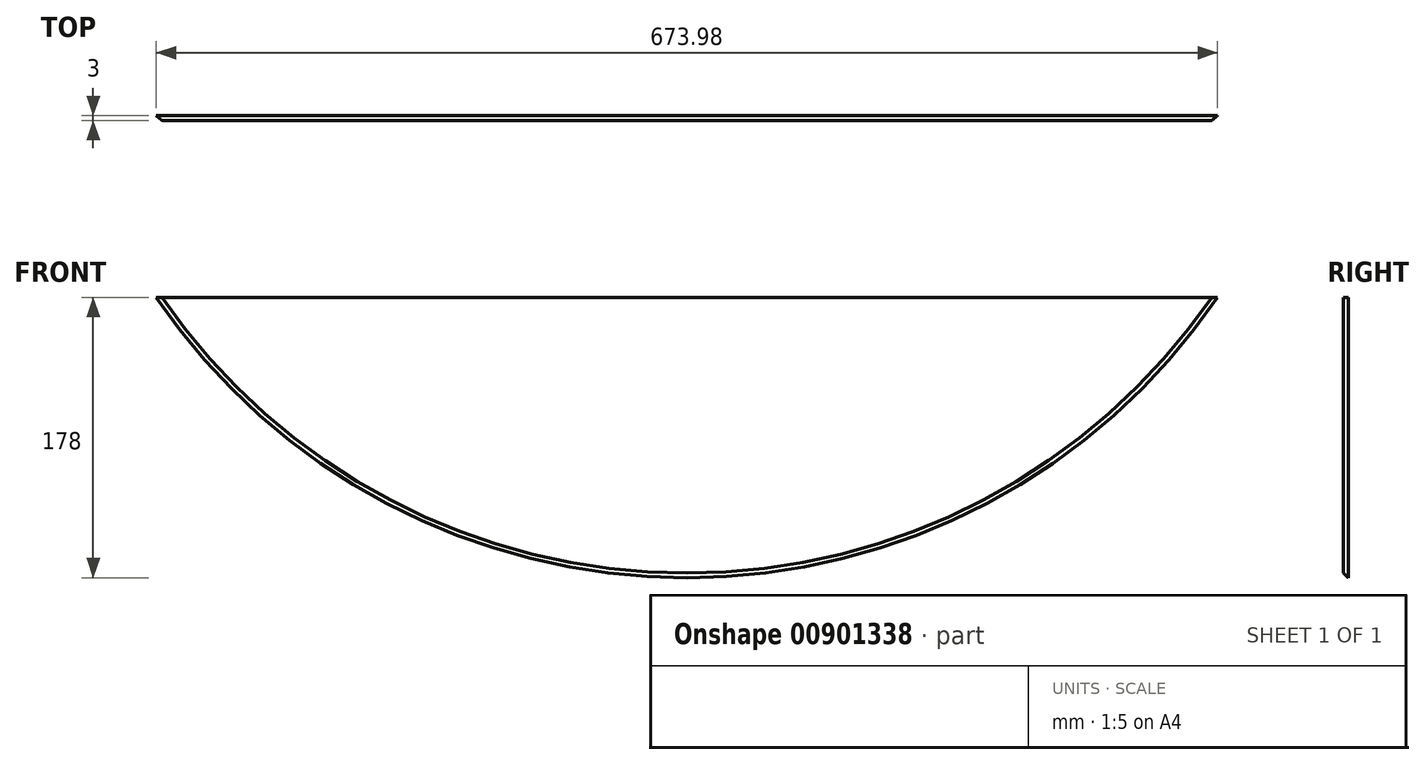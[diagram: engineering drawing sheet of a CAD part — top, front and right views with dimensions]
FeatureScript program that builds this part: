
annotation { "Feature Type Name" : "Feature", "Feature Type Description" : "" }
export const myFeature = defineFeature(function(context is Context, id is Id, definition is map)
    precondition{}
    {
        {
            var Q0;
            Q0=qCreatedBy(makeId("Front.planeOp"),FACE);
            var sketch = newSketch(context, id + "F0", { "sketchPlane" : qUnion([Q0])});
            skArc(sketch, "E0", {"start": v(-339.41, 0) * mm, "mid": v(0, -180) * mm, "end": v(339.41, 0) * mm});
            skLineSegment(sketch, "E1", {"start": v(0, 0) * mm, "end": v(-339.41, 0) * mm});
            skLineSegment(sketch, "E2", {"start": v(0, 0) * mm, "end": v(339.41, 0) * mm});
            skLineSegment(sketch, "E3", {"start": v(-339.41, 0) * mm, "end": v(-199.41, 0) * mm});
            skLineSegment(sketch, "E4", {"start": v(339.41, 0) * mm, "end": v(199.41, 0) * mm});
            skLineSegment(sketch, "E5", {"start": v(-199.41, 0) * mm, "end": v(-199.41, 45) * mm});
            skCircle(sketch, "E6", {"center": v(-199.41, 45) * mm, "radius": 17.5 * mm});
            skLineSegment(sketch, "E7", {"start": v(-199.41, 0) * mm, "end": v(-199.41, -45) * mm});
            skLineSegment(sketch, "E8", {"start": v(-199.41, -45) * mm, "end": v(-269.41, -45) * mm});
            skLineSegment(sketch, "E9", {"start": v(-199.41, -45) * mm, "end": v(-129.41, -45) * mm});
            skLineSegment(sketch, "E10", {"start": v(-129.41, -45) * mm, "end": v(-184.11, 53.5) * mm});
            skLineSegment(sketch, "E11", {"start": v(-269.41, -45) * mm, "end": v(-214.71, 53.5) * mm});
            skCircle(sketch, "E12", {"center": v(-239.67, -27.5) * mm, "radius": 17.5 * mm});
            skCircle(sketch, "E13", {"center": v(-159.15, -27.5) * mm, "radius": 17.5 * mm});
            skLineSegment(sketch, "E14", {"start": v(199.41, 0) * mm, "end": v(199.41, 45) * mm});
            skCircle(sketch, "E15", {"center": v(199.41, 45) * mm, "radius": 17.5 * mm});
            skLineSegment(sketch, "E16", {"start": v(199.41, 0) * mm, "end": v(199.41, -45) * mm});
            skLineSegment(sketch, "E17", {"start": v(199.41, -45) * mm, "end": v(129.41, -45) * mm});
            skLineSegment(sketch, "E18", {"start": v(199.41, -45) * mm, "end": v(269.41, -45) * mm});
            skLineSegment(sketch, "E19", {"start": v(269.41, -45) * mm, "end": v(214.71, 53.5) * mm});
            skLineSegment(sketch, "E20", {"start": v(129.41, -45) * mm, "end": v(184.11, 53.5) * mm});
            skCircle(sketch, "E21", {"center": v(159.15, -27.5) * mm, "radius": 17.5 * mm});
            skCircle(sketch, "E22", {"center": v(239.67, -27.5) * mm, "radius": 17.5 * mm});
            skSolve(sketch);
        }
        {
            var Q0;
            {var subQ23=sQuery(id+"F0.wireOp",EDGE,"E0");Q0=makeQuery(id+"F0.imprint","IMPRINT",FACE,{"disambiguationData":[TD([[makeQuery(id+"F0.imprint","IMPRINT",EDGE,{"derivedFrom":subQ23}),1.0]])]});}
            var Q1;
            {var subQ0=sQuery(id+"F0.wireOp",EDGE,"E11");var subQ1=sQuery(id+"F0.wireOp",EDGE,"E8");var subQ2=makeQuery(id+"F0.imprint","INTERSECT",VERTEX,{"derivedFrom":[subQ1,subQ0]});Q1=makeQuery(id+"F0.imprint","IMPRINT",FACE,{"disambiguationData":[TD([[makeQuery(id+"F0.imprint","IMPRINT",EDGE,{"disambiguationData":[TD([[subQ2,1.0]])],"derivedFrom":subQ1}),-1.0]])]});}
            var Q2;
            {var subQ0=sQuery(id+"F0.wireOp",EDGE,"E10");var subQ1=sQuery(id+"F0.wireOp",EDGE,"E9");var subQ2=makeQuery(id+"F0.imprint","INTERSECT",VERTEX,{"derivedFrom":[subQ1,subQ0]});Q2=makeQuery(id+"F0.imprint","IMPRINT",FACE,{"disambiguationData":[TD([[makeQuery(id+"F0.imprint","IMPRINT",EDGE,{"disambiguationData":[TD([[subQ2,1.0]])],"derivedFrom":subQ1}),1.0]])]});}
            var Q3;
            {var subQ0=sQuery(id+"F0.wireOp",EDGE,"E20");var subQ1=sQuery(id+"F0.wireOp",EDGE,"E17");var subQ2=makeQuery(id+"F0.imprint","INTERSECT",VERTEX,{"derivedFrom":[subQ1,subQ0]});Q3=makeQuery(id+"F0.imprint","IMPRINT",FACE,{"disambiguationData":[TD([[makeQuery(id+"F0.imprint","IMPRINT",EDGE,{"disambiguationData":[TD([[subQ2,1.0]])],"derivedFrom":subQ1}),-1.0]])]});}
            var Q4;
            {var subQ0=sQuery(id+"F0.wireOp",EDGE,"E19");var subQ1=sQuery(id+"F0.wireOp",EDGE,"E18");var subQ2=makeQuery(id+"F0.imprint","INTERSECT",VERTEX,{"derivedFrom":[subQ1,subQ0]});Q4=makeQuery(id+"F0.imprint","IMPRINT",FACE,{"disambiguationData":[TD([[makeQuery(id+"F0.imprint","IMPRINT",EDGE,{"disambiguationData":[TD([[subQ2,1.0]])],"derivedFrom":subQ1}),1.0]])]});}
            var Q5;
            {var subQ0=sQuery(id+"F0.wireOp",EDGE,"E21");var subQ1=makeQuery(id+"F0.imprint","INTERSECT",VERTEX,{"derivedFrom":[sQuery(id+"F0.wireOp",EDGE,"E17"),subQ0]});Q5=makeQuery(id+"F0.imprint","IMPRINT",FACE,{"disambiguationData":[TD([[makeQuery(id+"F0.imprint","IMPRINT",EDGE,{"disambiguationData":[TD([[subQ1,1.0]])],"derivedFrom":subQ0}),1.0]])]});}
            var Q6;
            {var subQ6=sQuery(id+"F0.wireOp",EDGE,"E16");Q6=makeQuery(id+"F0.imprint","IMPRINT",FACE,{"disambiguationData":[TD([[makeQuery(id+"F0.imprint","IMPRINT",EDGE,{"derivedFrom":subQ6}),-1.0]])]});}
            var Q7;
            {var subQ1=sQuery(id+"F0.wireOp",EDGE,"E16");Q7=makeQuery(id+"F0.imprint","IMPRINT",FACE,{"disambiguationData":[TD([[makeQuery(id+"F0.imprint","IMPRINT",EDGE,{"derivedFrom":subQ1}),1.0]])]});}
            var Q8;
            {var subQ0=sQuery(id+"F0.wireOp",EDGE,"E22");var subQ1=makeQuery(id+"F0.imprint","INTERSECT",VERTEX,{"derivedFrom":[sQuery(id+"F0.wireOp",EDGE,"E18"),subQ0]});Q8=makeQuery(id+"F0.imprint","IMPRINT",FACE,{"disambiguationData":[TD([[makeQuery(id+"F0.imprint","IMPRINT",EDGE,{"disambiguationData":[TD([[subQ1,1.0]])],"derivedFrom":subQ0}),1.0]])]});}
            var Q9;
            {var subQ0=sQuery(id+"F0.wireOp",EDGE,"E12");var subQ1=makeQuery(id+"F0.imprint","INTERSECT",VERTEX,{"derivedFrom":[sQuery(id+"F0.wireOp",EDGE,"E8"),subQ0]});Q9=makeQuery(id+"F0.imprint","IMPRINT",FACE,{"disambiguationData":[TD([[makeQuery(id+"F0.imprint","IMPRINT",EDGE,{"disambiguationData":[TD([[subQ1,1.0]])],"derivedFrom":subQ0}),1.0]])]});}
            var Q10;
            {var subQ6=sQuery(id+"F0.wireOp",EDGE,"E7");Q10=makeQuery(id+"F0.imprint","IMPRINT",FACE,{"disambiguationData":[TD([[makeQuery(id+"F0.imprint","IMPRINT",EDGE,{"derivedFrom":subQ6}),-1.0]])]});}
            var Q11;
            {var subQ6=sQuery(id+"F0.wireOp",EDGE,"E7");Q11=makeQuery(id+"F0.imprint","IMPRINT",FACE,{"disambiguationData":[TD([[makeQuery(id+"F0.imprint","IMPRINT",EDGE,{"derivedFrom":subQ6}),1.0]])]});}
            var Q12;
            {var subQ0=sQuery(id+"F0.wireOp",EDGE,"E13");var subQ1=makeQuery(id+"F0.imprint","INTERSECT",VERTEX,{"derivedFrom":[sQuery(id+"F0.wireOp",EDGE,"E9"),subQ0]});Q12=makeQuery(id+"F0.imprint","IMPRINT",FACE,{"disambiguationData":[TD([[makeQuery(id+"F0.imprint","IMPRINT",EDGE,{"disambiguationData":[TD([[subQ1,1.0]])],"derivedFrom":subQ0}),1.0]])]});}
            extrude(context, id + "F1", {"entities" : qUnion([Q0, Q1, Q2, Q3, Q4, Q5, Q6, Q7, Q8, Q9, Q10, Q11, Q12]), "endBound" : BoundingType.SYMMETRIC, "depth" : 3 * mm, "offsetDistance" : 25 * mm});
        }
        {
            var Q0;
            Q0=makeQuery(id+"F1.opExtrude","CAP_EDGE",EDGE,{"disambiguationData":[OSD([sQuery(id+"F0.wireOp",EDGE,"E0")])],"isStart":false});
            chamfer(context, id + "F2", {"entities" : qUnion([Q0]), "width" : 5 * mm, "tangentPropagation" : true});
        }
    });
